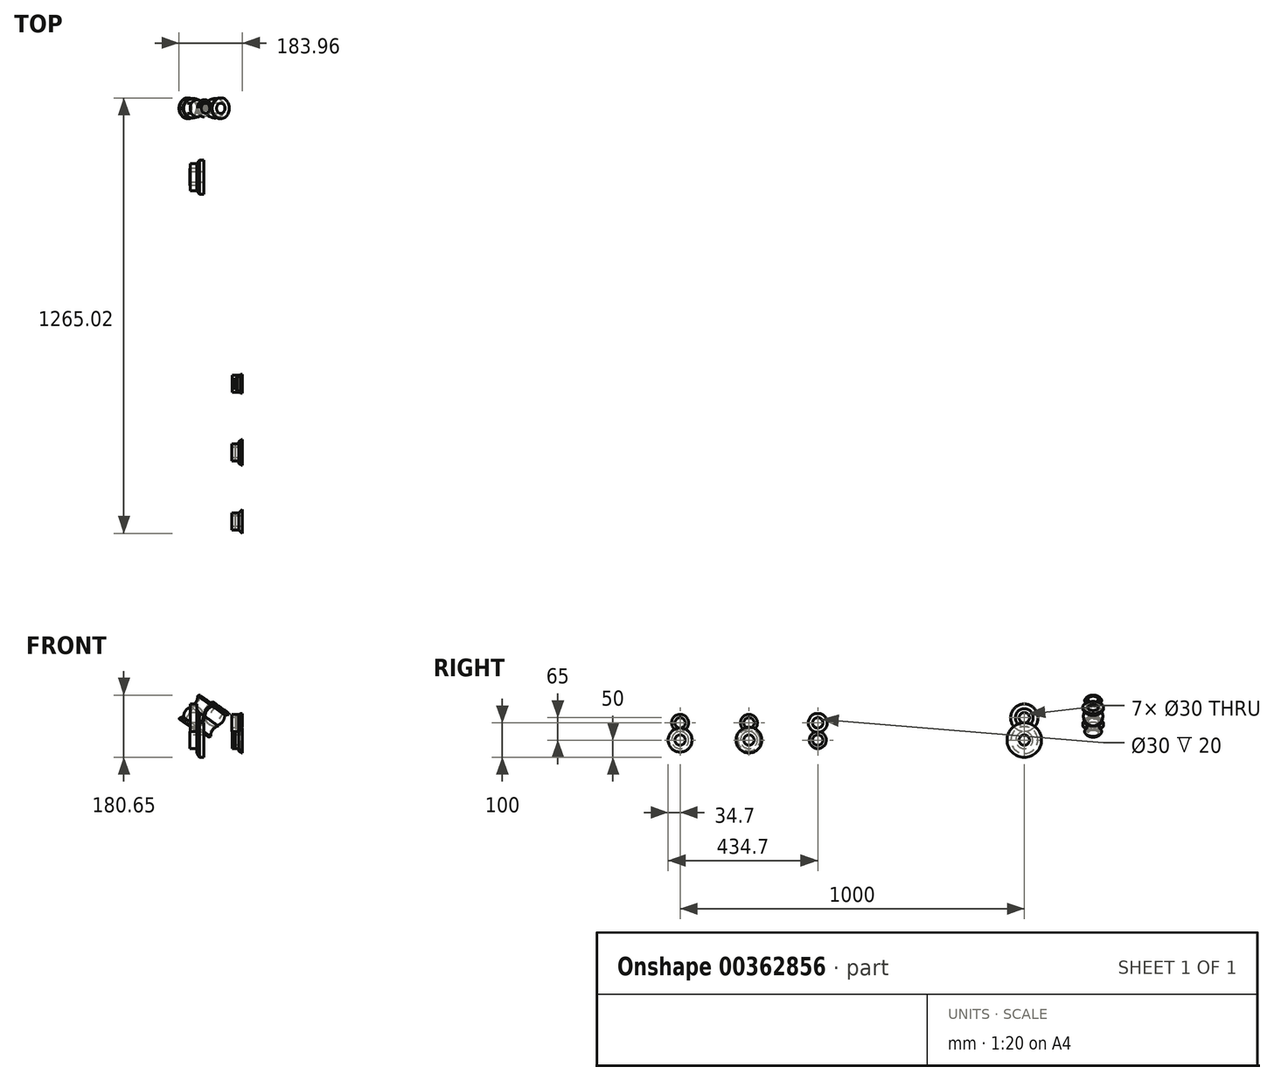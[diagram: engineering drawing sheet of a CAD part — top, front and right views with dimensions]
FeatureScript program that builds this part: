
annotation { "Feature Type Name" : "Feature", "Feature Type Description" : "" }
export const myFeature = defineFeature(function(context is Context, id is Id, definition is map)
    precondition{}
    {
        {
            var Q0;
            Q0=qCreatedBy(makeId("Front.planeOp"),FACE);
            cPlane(context, id + "F0", {"entities" : qUnion([Q0]), "cplaneType" : CPlaneType.OFFSET, "offset" : 200 * mm, "oppositeDirection" : true, "width" : 150 * mm, "height" : 150 * mm});
        }
        {
            var Q0;
            Q0=qCreatedBy(id+"F0.planeOp",FACE);
            cPlane(context, id + "F1", {"entities" : qUnion([Q0]), "cplaneType" : CPlaneType.OFFSET, "offset" : 200 * mm, "oppositeDirection" : true, "width" : 150 * mm, "height" : 150 * mm});
        }
        {
            var Q0;
            Q0=qCreatedBy(id+"F1.planeOp",FACE);
            cPlane(context, id + "F2", {"entities" : qUnion([Q0]), "cplaneType" : CPlaneType.OFFSET, "offset" : 200 * mm, "oppositeDirection" : true, "width" : 150 * mm, "height" : 150 * mm});
        }
        {
            var Q0;
            Q0=qCreatedBy(id+"F2.planeOp",FACE);
            cPlane(context, id + "F3", {"entities" : qUnion([Q0]), "cplaneType" : CPlaneType.OFFSET, "offset" : 200 * mm, "oppositeDirection" : true, "width" : 150 * mm, "height" : 150 * mm});
        }
        {
            var Q0;
            Q0=qCreatedBy(id+"F3.planeOp",FACE);
            cPlane(context, id + "F4", {"entities" : qUnion([Q0]), "cplaneType" : CPlaneType.OFFSET, "offset" : 200 * mm, "oppositeDirection" : true, "width" : 150 * mm, "height" : 150 * mm});
        }
        {
            var Q0;
            Q0=qCreatedBy(id+"F4.planeOp",FACE);
            cPlane(context, id + "F5", {"entities" : qUnion([Q0]), "cplaneType" : CPlaneType.OFFSET, "offset" : 200 * mm, "oppositeDirection" : true, "width" : 150 * mm, "height" : 150 * mm});
        }
        {
            var Q0;
            Q0=qCreatedBy(id+"F5.planeOp",FACE);
            cPlane(context, id + "F6", {"entities" : qUnion([Q0]), "cplaneType" : CPlaneType.OFFSET, "offset" : 200 * mm, "oppositeDirection" : true, "width" : 150 * mm, "height" : 150 * mm});
        }
        {
            var Q0;
            Q0=qCreatedBy(id+"F6.planeOp",FACE);
            cPlane(context, id + "F7", {"entities" : qUnion([Q0]), "cplaneType" : CPlaneType.OFFSET, "offset" : 200 * mm, "oppositeDirection" : true, "width" : 150 * mm, "height" : 150 * mm});
        }
        {
            var Q0;
            Q0=qCreatedBy(id+"F7.planeOp",FACE);
            cPlane(context, id + "F8", {"entities" : qUnion([Q0]), "cplaneType" : CPlaneType.OFFSET, "offset" : 200 * mm, "oppositeDirection" : true, "width" : 150 * mm, "height" : 150 * mm});
        }
        {
            var Q0;
            Q0=qCreatedBy(id+"F0.planeOp",FACE);
            var sketch = newSketch(context, id + "F9", { "sketchPlane" : qUnion([Q0])});
            skLineSegment(sketch, "E0", {"start": v(0, 0) * mm, "end": v(206, 0) * mm});
            skLineSegment(sketch, "E1", {"start": v(0, 0) * mm, "end": v(-89, 0) * mm});
            skLineSegment(sketch, "E2", {"start": v(206, 0) * mm, "end": v(210.24, 4.24) * mm});
            skLineSegment(sketch, "E3", {"start": v(-89, 0) * mm, "end": v(-93.95, 4.95) * mm});
            skLineSegment(sketch, "E4.0", {"start": v(206.12, -0.3) * mm, "end": v(210.45, 4.03) * mm});
            skLineSegment(sketch, "E4.1", {"start": v(0, -0.3) * mm, "end": v(206.12, -0.3) * mm});
            skLineSegment(sketch, "E4.2", {"start": v(0, -0.3) * mm, "end": v(-89.12, -0.3) * mm});
            skLineSegment(sketch, "E4.3", {"start": v(-89.12, -0.3) * mm, "end": v(-94.16, 4.74) * mm});
            skLineSegment(sketch, "E5.0", {"start": v(205.88, 0.3) * mm, "end": v(210.03, 4.45) * mm});
            skLineSegment(sketch, "E5.1", {"start": v(0, 0.3) * mm, "end": v(205.88, 0.3) * mm});
            skLineSegment(sketch, "E5.2", {"start": v(0, 0.3) * mm, "end": v(-88.88, 0.3) * mm});
            skLineSegment(sketch, "E5.3", {"start": v(-88.88, 0.3) * mm, "end": v(-93.74, 5.16) * mm});
            skLineSegment(sketch, "E6", {"start": v(196.12, -0.3) * mm, "end": v(196.12, -10) * mm});
            skLineSegment(sketch, "E7", {"start": v(196.12, -10) * mm, "end": v(216.12, -10) * mm});
            skLineSegment(sketch, "E8", {"start": v(216.12, -10) * mm, "end": v(216.12, 9.7) * mm});
            skLineSegment(sketch, "E9", {"start": v(210.45, 4.03) * mm, "end": v(216.12, 9.7) * mm});
            skLineSegment(sketch, "E10", {"start": v(173.5, -25) * mm, "end": v(260.17, -25) * mm, "construction": true});
            skLineSegment(sketch, "E11", {"start": v(185.88, 0.3) * mm, "end": v(185.88, 10) * mm});
            skLineSegment(sketch, "E12", {"start": v(185.88, 10) * mm, "end": v(205.88, 10) * mm});
            skLineSegment(sketch, "E13", {"start": v(205.88, 10) * mm, "end": v(205.88, 0.3) * mm});
            skLineSegment(sketch, "E14", {"start": v(171.99, 25) * mm, "end": v(233.28, 25) * mm, "construction": true});
            skSolve(sketch);
        }
        {
            var Q0;
            Q0=qCreatedBy(id+"F1.planeOp",FACE);
            var sketch = newSketch(context, id + "F10", { "sketchPlane" : qUnion([Q0])});
            skLineSegment(sketch, "E15.0", {"start": v(171.99, 25) * mm, "end": v(233.28, 25) * mm, "construction": true});
            skLineSegment(sketch, "E16.0", {"start": v(173.5, -25) * mm, "end": v(260.17, -25) * mm, "construction": true});
            skLineSegment(sketch, "E17.0", {"start": v(196.12, -0.3) * mm, "end": v(196.12, -10) * mm});
            skLineSegment(sketch, "E18", {"start": v(196.12, -0.3) * mm, "end": v(206.12, -0.3) * mm});
            skLineSegment(sketch, "E19", {"start": v(206.12, -0.3) * mm, "end": v(206.12, 6.7) * mm});
            skLineSegment(sketch, "E20", {"start": v(206.12, 6.7) * mm, "end": v(213.12, 12.5) * mm});
            skLineSegment(sketch, "E21.0", {"start": v(196.12, -10) * mm, "end": v(216.12, -10) * mm});
            skPoint(sketch, "E22.orphan", {"position": v(208.77, 12.5) * mm});
            skLineSegment(sketch, "E23.bottom", {"start": v(205.52, 0.3) * mm, "end": v(185.52, 0.3) * mm});
            skLineSegment(sketch, "E23.top", {"start": v(205.52, 10) * mm, "end": v(185.52, 10) * mm});
            skLineSegment(sketch, "E23.left", {"start": v(205.52, 0.3) * mm, "end": v(205.52, 10) * mm});
            skLineSegment(sketch, "E23.right", {"start": v(185.52, 0.3) * mm, "end": v(185.52, 10) * mm});
            skLineSegment(sketch, "E24", {"start": v(216.12, -10) * mm, "end": v(216.12, 12.5) * mm});
            skLineSegment(sketch, "E25", {"start": v(213.12, 12.5) * mm, "end": v(216.12, 12.5) * mm});
            skSolve(sketch);
        }
        {
            var Q0;
            Q0=qCreatedBy(id+"F2.planeOp",FACE);
            var sketch = newSketch(context, id + "F11", { "sketchPlane" : qUnion([Q0])});
            skLineSegment(sketch, "E26", {"start": v(211.05, -2.5) * mm, "end": v(201.05, 7.5) * mm});
            skLineSegment(sketch, "E27", {"start": v(211.05, -2.5) * mm, "end": v(216.05, -2.5) * mm});
            skLineSegment(sketch, "E28", {"start": v(216.05, -2.5) * mm, "end": v(216.05, 10) * mm});
            skLineSegment(sketch, "E29", {"start": v(216.05, 10) * mm, "end": v(196.05, 10) * mm});
            skLineSegment(sketch, "E30", {"start": v(196.05, 10) * mm, "end": v(196.05, 7.5) * mm});
            skLineSegment(sketch, "E31", {"start": v(196.05, 7.5) * mm, "end": v(201.05, 7.5) * mm});
            skLineSegment(sketch, "E32.0", {"start": v(171.99, 25) * mm, "end": v(233.28, 25) * mm, "construction": true});
            skLineSegment(sketch, "E33.0", {"start": v(173.5, -25) * mm, "end": v(260.17, -25) * mm, "construction": true});
            skLineSegment(sketch, "E34.bottom", {"start": v(187.12, -10) * mm, "end": v(207.12, -10) * mm});
            skLineSegment(sketch, "E34.top", {"start": v(187.12, -0.3) * mm, "end": v(207.12, -0.3) * mm});
            skLineSegment(sketch, "E34.left", {"start": v(187.12, -10) * mm, "end": v(187.12, -0.3) * mm});
            skLineSegment(sketch, "E34.right", {"start": v(207.12, -10) * mm, "end": v(207.12, -0.3) * mm});
            skSolve(sketch);
        }
        {
            var Q0;
            Q0=qCreatedBy(id+"F3.planeOp",FACE);
            var sketch = newSketch(context, id + "F12", { "sketchPlane" : qUnion([Q0])});
            skLineSegment(sketch, "E35.0", {"start": v(207.12, -10) * mm, "end": v(207.12, -0.3) * mm});
            skLineSegment(sketch, "E36.0", {"start": v(187.12, -0.3) * mm, "end": v(207.12, -0.3) * mm});
            skLineSegment(sketch, "E37.0", {"start": v(187.12, -10) * mm, "end": v(187.12, -0.3) * mm});
            skLineSegment(sketch, "E38.0", {"start": v(187.12, -10) * mm, "end": v(207.12, -10) * mm});
            skLineSegment(sketch, "E39.0", {"start": v(171.99, 25) * mm, "end": v(233.28, 25) * mm, "construction": true});
            skLineSegment(sketch, "E40.0", {"start": v(173.5, -25) * mm, "end": v(260.17, -25) * mm, "construction": true});
            skLineSegment(sketch, "E41", {"start": v(196.08, 4.48) * mm, "end": v(209.08, 1) * mm});
            skLineSegment(sketch, "E42", {"start": v(196.08, 4.48) * mm, "end": v(196.08, 9.86) * mm});
            skLineSegment(sketch, "E43", {"start": v(196.08, 9.86) * mm, "end": v(216.08, 9.86) * mm});
            skLineSegment(sketch, "E44", {"start": v(216.08, 9.86) * mm, "end": v(216.08, 1) * mm});
            skLineSegment(sketch, "E45", {"start": v(216.08, 1) * mm, "end": v(209.08, 1) * mm});
            skSolve(sketch);
        }
        {
            var Q0;
            Q0=qCreatedBy(id+"F4.planeOp",FACE);
            var sketch = newSketch(context, id + "F13", { "sketchPlane" : qUnion([Q0])});
            skLineSegment(sketch, "E46", {"start": v(0, 0) * mm, "end": v(84, 0) * mm});
            skLineSegment(sketch, "E47", {"start": v(84, 0) * mm, "end": v(174.5, 90.5) * mm});
            skLineSegment(sketch, "E48", {"start": v(0, 0) * mm, "end": v(-62.93, 62.93) * mm});
            skLineSegment(sketch, "E49.0", {"start": v(84.12, -0.3) * mm, "end": v(174.72, 90.3) * mm});
            skLineSegment(sketch, "E49.1", {"start": v(-0.12, -0.3) * mm, "end": v(84.12, -0.3) * mm});
            skLineSegment(sketch, "E49.2", {"start": v(-0.12, -0.3) * mm, "end": v(-63.14, 62.72) * mm});
            skLineSegment(sketch, "E50.0", {"start": v(0.12, 0.3) * mm, "end": v(-62.72, 63.14) * mm});
            skLineSegment(sketch, "E50.1", {"start": v(0.12, 0.3) * mm, "end": v(83.88, 0.3) * mm});
            skLineSegment(sketch, "E50.2", {"start": v(83.88, 0.3) * mm, "end": v(174.3, 90.72) * mm});
            skLineSegment(sketch, "E51", {"start": v(64.12, -0.3) * mm, "end": v(64.12, -10) * mm});
            skLineSegment(sketch, "E52", {"start": v(64.12, -10) * mm, "end": v(104.12, -10) * mm});
            skLineSegment(sketch, "E53", {"start": v(104.12, -10) * mm, "end": v(104.12, 19.7) * mm});
            skLineSegment(sketch, "E54.0", {"start": v(173.5, -25) * mm, "end": v(260.17, -25) * mm, "construction": true});
            skLineSegment(sketch, "E55.0", {"start": v(171.99, 25) * mm, "end": v(233.28, 25) * mm, "construction": true});
            skLineSegment(sketch, "E56.bottom", {"start": v(63.88, 10) * mm, "end": v(83.88, 10) * mm});
            skLineSegment(sketch, "E56.top", {"start": v(63.88, 0.3) * mm, "end": v(83.88, 0.3) * mm});
            skLineSegment(sketch, "E56.left", {"start": v(63.88, 10) * mm, "end": v(63.88, 0.3) * mm});
            skLineSegment(sketch, "E56.right", {"start": v(83.88, 10) * mm, "end": v(83.88, 0.3) * mm});
            skSolve(sketch);
        }
        {
            var Q0;
            Q0=qCreatedBy(id+"F5.planeOp",FACE);
            var sketch = newSketch(context, id + "F14", { "sketchPlane" : qUnion([Q0])});
            skLineSegment(sketch, "E57", {"start": v(0, 0) * mm, "end": v(83.7, 0) * mm});
            skLineSegment(sketch, "E58", {"start": v(83.7, 0) * mm, "end": v(83.7, 14) * mm});
            skLineSegment(sketch, "E59", {"start": v(83.7, 14) * mm, "end": v(149.41, 107.15) * mm});
            skLineSegment(sketch, "E60", {"start": v(0, 0) * mm, "end": v(0, 89) * mm});
            skLineSegment(sketch, "E61.0", {"start": v(84, 13.9) * mm, "end": v(149.66, 106.98) * mm});
            skLineSegment(sketch, "E61.1", {"start": v(84, -0.3) * mm, "end": v(84, 13.9) * mm});
            skLineSegment(sketch, "E61.2", {"start": v(-0.3, -0.3) * mm, "end": v(84, -0.3) * mm});
            skLineSegment(sketch, "E61.3", {"start": v(-0.3, -0.3) * mm, "end": v(-0.3, 89) * mm});
            skLineSegment(sketch, "E62.0", {"start": v(0.3, 0.3) * mm, "end": v(0.3, 89) * mm});
            skLineSegment(sketch, "E62.1", {"start": v(0.3, 0.3) * mm, "end": v(83.4, 0.3) * mm});
            skLineSegment(sketch, "E62.2", {"start": v(83.4, 0.3) * mm, "end": v(83.4, 14.1) * mm});
            skLineSegment(sketch, "E62.3", {"start": v(83.4, 14.1) * mm, "end": v(149.17, 107.33) * mm});
            skLineSegment(sketch, "E63", {"start": v(64, -0.3) * mm, "end": v(64, -10) * mm});
            skLineSegment(sketch, "E64", {"start": v(64, -10) * mm, "end": v(104, -10) * mm});
            skLineSegment(sketch, "E65", {"start": v(104, -10) * mm, "end": v(104, 25) * mm});
            skLineSegment(sketch, "E66", {"start": v(104, 25) * mm, "end": v(91.83, 25) * mm});
            skLineSegment(sketch, "E67.0", {"start": v(173.5, -25) * mm, "end": v(260.17, -25) * mm, "construction": true});
            skLineSegment(sketch, "E68", {"start": v(64.37, 0.3) * mm, "end": v(64.37, 25) * mm});
            skLineSegment(sketch, "E69", {"start": v(64.37, 25) * mm, "end": v(91.1, 25) * mm});
            skLineSegment(sketch, "E70", {"start": v(50.32, 40) * mm, "end": v(125.83, 40) * mm, "construction": true});
            skLineSegment(sketch, "E71", {"start": v(0.3, 25) * mm, "end": v(20.3, 25) * mm});
            skLineSegment(sketch, "E72", {"start": v(20.3, 25) * mm, "end": v(20.3, 0.3) * mm});
            skSolve(sketch);
        }
        {
            var Q0;
            Q0=qCreatedBy(id+"F6.planeOp",FACE);
            var sketch = newSketch(context, id + "F15", { "sketchPlane" : qUnion([Q0])});
            skLineSegment(sketch, "E73", {"start": v(0, 0) * mm, "end": v(83.7, 0) * mm});
            skLineSegment(sketch, "E74", {"start": v(83.7, 0) * mm, "end": v(83.7, 14) * mm});
            skLineSegment(sketch, "E75", {"start": v(83.7, 14) * mm, "end": v(126.7, 75) * mm, "construction": true});
            skLineSegment(sketch, "E76", {"start": v(0, 0) * mm, "end": v(0, 89) * mm});
            skArc(sketch, "E77", {"start": v(83.7, 14) * mm, "mid": v(99.77, 25.5) * mm, "end": v(105.2, 44.5) * mm});
            skArc(sketch, "E78", {"start": v(126.7, 75) * mm, "mid": v(110.64, 63.5) * mm, "end": v(105.2, 44.5) * mm});
            skLineSegment(sketch, "E79", {"start": v(126.7, 75) * mm, "end": v(126.7, 109) * mm});
            skLineSegment(sketch, "E80.0", {"start": v(127, 74.77) * mm, "end": v(127, 109) * mm});
            skArc(sketch, "E80.1", {"start": v(127, 74.77) * mm, "mid": v(110.95, 63.41) * mm, "end": v(105.5, 44.51) * mm});
            skLineSegment(sketch, "E80.2", {"start": v(-0.3, -0.3) * mm, "end": v(-0.3, 77.26) * mm});
            skLineSegment(sketch, "E80.3", {"start": v(-0.3, -0.3) * mm, "end": v(84, -0.3) * mm});
            skLineSegment(sketch, "E80.4", {"start": v(84, -0.3) * mm, "end": v(84, 13.78) * mm});
            skArc(sketch, "E80.5", {"start": v(84, 13.78) * mm, "mid": v(100.08, 25.42) * mm, "end": v(105.5, 44.51) * mm});
            skLineSegment(sketch, "E81.0", {"start": v(126.4, 75.22) * mm, "end": v(126.4, 109) * mm});
            skArc(sketch, "E81.1", {"start": v(126.4, 75.22) * mm, "mid": v(110.33, 63.58) * mm, "end": v(104.9, 44.48) * mm});
            skLineSegment(sketch, "E81.2", {"start": v(0.3, 0.3) * mm, "end": v(0.3, 77.26) * mm});
            skLineSegment(sketch, "E81.3", {"start": v(0.3, 0.3) * mm, "end": v(83.4, 0.3) * mm});
            skLineSegment(sketch, "E81.4", {"start": v(83.4, 0.3) * mm, "end": v(83.4, 14.23) * mm});
            skArc(sketch, "E81.5", {"start": v(83.4, 14.23) * mm, "mid": v(99.46, 25.58) * mm, "end": v(104.9, 44.48) * mm});
            skLineSegment(sketch, "E82", {"start": v(141.21, 78.21) * mm, "end": v(88.99, 4.14) * mm});
            skLineSegment(sketch, "E83", {"start": v(88.99, 4.14) * mm, "end": v(84, 7.66) * mm});
            skLineSegment(sketch, "E84", {"start": v(89.66, -20.93) * mm, "end": v(174.5, 99.37) * mm, "construction": true});
            skLineSegment(sketch, "E85", {"start": v(127, 84.65) * mm, "end": v(128.7, 87.04) * mm});
            skLineSegment(sketch, "E86", {"start": v(128.7, 87.04) * mm, "end": v(141.21, 78.21) * mm});
            skLineSegment(sketch, "E87.1.0", {"start": v(83.4, 4.34) * mm, "end": v(81.72, 1.95) * mm});
            skLineSegment(sketch, "E87.1.1", {"start": v(81.72, 1.95) * mm, "end": v(69.2, 10.78) * mm});
            skLineSegment(sketch, "E87.1.2", {"start": v(69.2, 10.78) * mm, "end": v(121.42, 84.85) * mm});
            skLineSegment(sketch, "E87.1.3", {"start": v(121.42, 84.85) * mm, "end": v(126.4, 81.33) * mm});
            skPoint(sketch, "E87.center", {"position": v(105.2, 44.5) * mm});
            skLineSegment(sketch, "E87.anchor1", {"start": v(105.2, 44.5) * mm, "end": v(127, 84.65) * mm, "construction": true});
            skLineSegment(sketch, "E87.anchor2", {"start": v(105.2, 44.5) * mm, "end": v(83.4, 4.34) * mm, "construction": true});
            skLineSegment(sketch, "E88.MirrorCS", {"start": v(48.8, 7.89) * mm, "end": v(133.63, 128.19) * mm, "construction": true});
            skLineSegment(sketch, "E89.MirrorCS", {"start": v(44.68, 28.07) * mm, "end": v(96.9, 102.14) * mm});
            skSolve(sketch);
        }
        {
            var Q0;
            Q0=qCreatedBy(id+"F7.planeOp",FACE);
            var sketch = newSketch(context, id + "F16", { "sketchPlane" : qUnion([Q0])});
            skLineSegment(sketch, "E90", {"start": v(126.7, 75) * mm, "end": v(126.7, 89) * mm});
            skLineSegment(sketch, "E91", {"start": v(126.7, 89) * mm, "end": v(116.81, 98.9) * mm});
            skLineSegment(sketch, "E92", {"start": v(116.81, 98.9) * mm, "end": v(119.81, 93.7) * mm});
            skLineSegment(sketch, "E93.0", {"start": v(115.41, 100.72) * mm, "end": v(119.55, 93.55) * mm});
            skLineSegment(sketch, "E93.1", {"start": v(127, 89.12) * mm, "end": v(115.41, 100.72) * mm});
            skLineSegment(sketch, "E93.2", {"start": v(127, 75) * mm, "end": v(127, 89.12) * mm});
            skLineSegment(sketch, "E94.0", {"start": v(118.2, 97.07) * mm, "end": v(120.07, 93.85) * mm});
            skLineSegment(sketch, "E94.1", {"start": v(126.4, 88.87) * mm, "end": v(118.2, 97.07) * mm});
            skLineSegment(sketch, "E94.2", {"start": v(126.4, 75.87) * mm, "end": v(126.4, 88.87) * mm});
            skLineSegment(sketch, "E95", {"start": v(126.4, 88.87) * mm, "end": v(116.7, 88.87) * mm});
            skLineSegment(sketch, "E96", {"start": v(116.7, 88.87) * mm, "end": v(116.7, 75.87) * mm});
            skLineSegment(sketch, "E97", {"start": v(116.7, 75.87) * mm, "end": v(126.4, 75.87) * mm});
            skLineSegment(sketch, "E98", {"start": v(101.7, 117.95) * mm, "end": v(101.7, 62.03) * mm, "construction": true});
            skLineSegment(sketch, "E99", {"start": v(151.7, 118.79) * mm, "end": v(151.7, 53.17) * mm, "construction": true});
            skLineSegment(sketch, "E100", {"start": v(127, 75) * mm, "end": v(136.7, 75) * mm});
            skLineSegment(sketch, "E101", {"start": v(136.7, 75) * mm, "end": v(136.7, 105.55) * mm});
            skLineSegment(sketch, "E102", {"start": v(136.7, 105.55) * mm, "end": v(115.41, 105.55) * mm});
            skLineSegment(sketch, "E103", {"start": v(115.41, 100.72) * mm, "end": v(115.41, 105.55) * mm});
            skSolve(sketch);
        }
        {
            var Q0;
            {var subQ2=sQuery(id+"F9.wireOp",EDGE,"E11");Q0=makeQuery(id+"F9.imprint","IMPRINT",FACE,{"disambiguationData":[TD([[makeQuery(id+"F9.imprint","IMPRINT",EDGE,{"derivedFrom":subQ2}),-1.0]])]});}
            var Q1;
            Q1=sQuery(id+"F9.wireOp",EDGE,"E14");
            revolve(context, id + "F17", {"entities" : qUnion([Q0]), "axis" : qUnion([Q1]), "revolveType" : RevolveType.FULL});
        }
        {
            var Q0;
            {var subQ2=sQuery(id+"F9.wireOp",EDGE,"E4.0");Q0=makeQuery(id+"F9.imprint","IMPRINT",FACE,{"disambiguationData":[TD([[makeQuery(id+"F9.imprint","IMPRINT",EDGE,{"derivedFrom":subQ2}),-1.0]])]});}
            var Q1;
            Q1=sQuery(id+"F9.wireOp",EDGE,"E10");
            revolve(context, id + "F18", {"entities" : qUnion([Q0]), "axis" : qUnion([Q1]), "revolveType" : RevolveType.FULL});
        }
        {
            var Q0;
            Q0=makeQuery(id+"F10.imprint","IMPRINT",FACE,{"disambiguationData":[TD([[makeQuery(id+"F10.imprint","IMPRINT",EDGE,{"derivedFrom":sQuery(id+"F10.wireOp",EDGE,"E17.0")}),1.0]])]});
            var Q1;
            Q1=sQuery(id+"F10.wireOp",EDGE,"E16.0");
            revolve(context, id + "F19", {"entities" : qUnion([Q0]), "axis" : qUnion([Q1]), "revolveType" : RevolveType.FULL});
        }
        {
            var Q0;
            Q0=makeQuery(id+"F10.imprint","IMPRINT",FACE,{"disambiguationData":[TD([[makeQuery(id+"F10.imprint","IMPRINT",EDGE,{"derivedFrom":sQuery(id+"F10.wireOp",EDGE,"E23.bottom")}),-1.0]])]});
            var Q1;
            Q1=sQuery(id+"F10.wireOp",EDGE,"E15.0");
            revolve(context, id + "F20", {"entities" : qUnion([Q0]), "axis" : qUnion([Q1]), "revolveType" : RevolveType.FULL});
        }
        {
            var Q0;
            Q0=makeQuery(id+"F11.imprint","IMPRINT",FACE,{"disambiguationData":[TD([[makeQuery(id+"F11.imprint","IMPRINT",EDGE,{"derivedFrom":sQuery(id+"F11.wireOp",EDGE,"E26")}),-1.0]])]});
            var Q1;
            Q1=sQuery(id+"F11.wireOp",EDGE,"E32.0");
            revolve(context, id + "F21", {"entities" : qUnion([Q0]), "axis" : qUnion([Q1]), "revolveType" : RevolveType.FULL});
        }
        {
            var Q0;
            Q0=makeQuery(id+"F11.imprint","IMPRINT",FACE,{"disambiguationData":[TD([[makeQuery(id+"F11.imprint","IMPRINT",EDGE,{"derivedFrom":sQuery(id+"F11.wireOp",EDGE,"E34.bottom")}),1.0]])]});
            var Q1;
            Q1=sQuery(id+"F11.wireOp",EDGE,"E33.0");
            revolve(context, id + "F22", {"entities" : qUnion([Q0]), "axis" : qUnion([Q1]), "revolveType" : RevolveType.FULL});
        }
        {
            var Q0;
            {var subQ2=sQuery(id+"F14.wireOp",EDGE,"E62.2");Q0=makeQuery(id+"F14.imprint","IMPRINT",FACE,{"disambiguationData":[TD([[makeQuery(id+"F14.imprint","IMPRINT",EDGE,{"derivedFrom":subQ2}),1.0]])]});}
            var Q1;
            Q1=sQuery(id+"F14.wireOp",EDGE,"E70");
            revolve(context, id + "F23", {"entities" : qUnion([Q0]), "axis" : qUnion([Q1]), "revolveType" : RevolveType.FULL});
        }
        {
            var Q0;
            {var subQ2=sQuery(id+"F14.wireOp",EDGE,"E61.1");Q0=makeQuery(id+"F14.imprint","IMPRINT",FACE,{"disambiguationData":[TD([[makeQuery(id+"F14.imprint","IMPRINT",EDGE,{"derivedFrom":subQ2}),-1.0]])]});}
            var Q1;
            Q1=sQuery(id+"F14.wireOp",EDGE,"E67.0");
            revolve(context, id + "F24", {"entities" : qUnion([Q0]), "axis" : qUnion([Q1]), "revolveType" : RevolveType.FULL});
        }
        {
            var Q0;
            {var subQ3=sQuery(id+"F15.wireOp",EDGE,"E81.1");Q0=makeQuery(id+"F15.imprint","IMPRINT",FACE,{"disambiguationData":[TD([[makeQuery(id+"F15.imprint","IMPRINT",EDGE,{"derivedFrom":subQ3}),-1.0]])]});}
            var Q1;
            Q1=sQuery(id+"F15.wireOp",EDGE,"E88.MirrorCS");
            revolve(context, id + "F25", {"entities" : qUnion([Q0]), "axis" : qUnion([Q1]), "revolveType" : RevolveType.FULL});
        }
        {
            var Q0;
            {var subQ3=sQuery(id+"F15.wireOp",EDGE,"E80.1");Q0=makeQuery(id+"F15.imprint","IMPRINT",FACE,{"disambiguationData":[TD([[makeQuery(id+"F15.imprint","IMPRINT",EDGE,{"derivedFrom":subQ3}),1.0]])]});}
            var Q1;
            Q1=sQuery(id+"F15.wireOp",EDGE,"E84");
            revolve(context, id + "F26", {"entities" : qUnion([Q0]), "axis" : qUnion([Q1]), "revolveType" : RevolveType.FULL});
        }
    });
